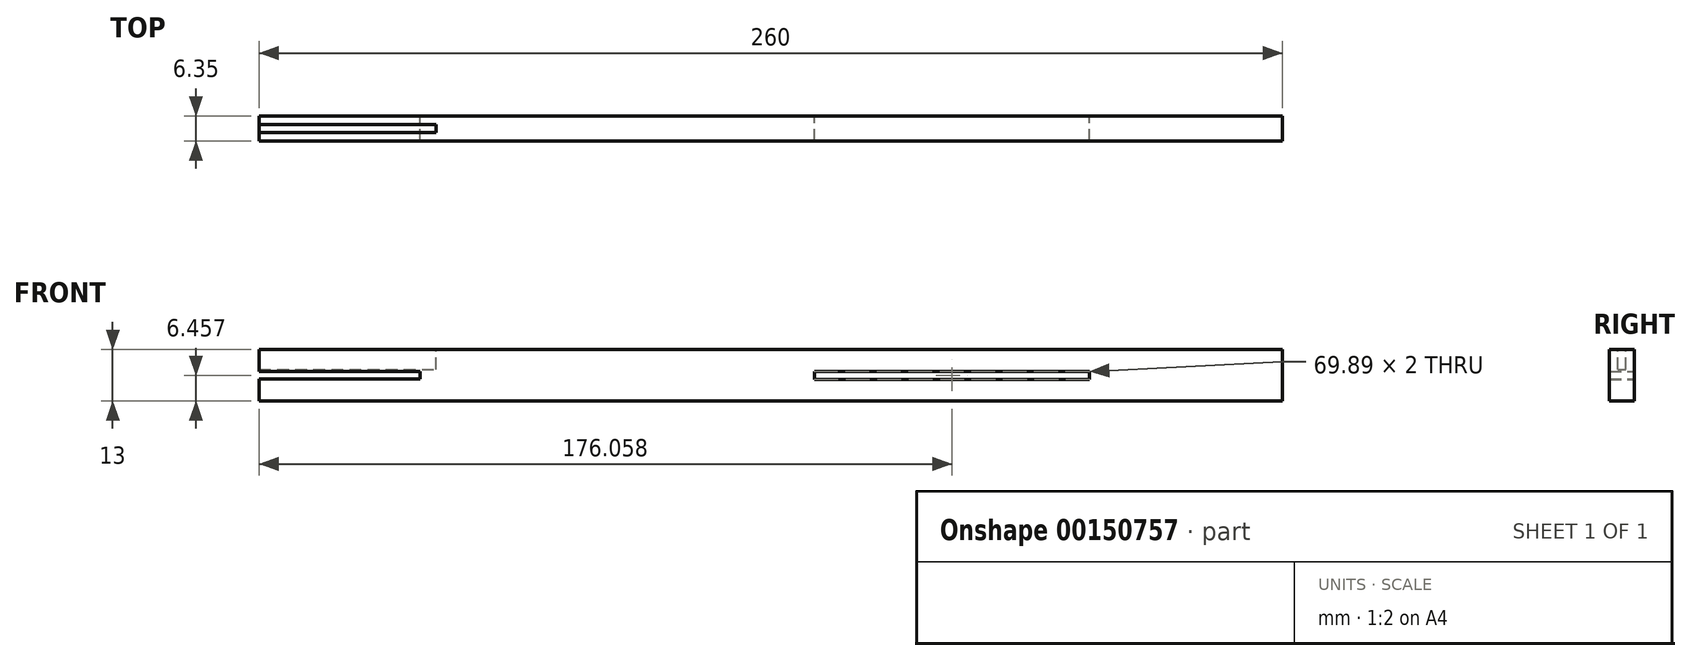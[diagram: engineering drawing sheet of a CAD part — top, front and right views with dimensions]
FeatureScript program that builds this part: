
annotation { "Feature Type Name" : "Feature", "Feature Type Description" : "" }
export const myFeature = defineFeature(function(context is Context, id is Id, definition is map)
    precondition{}
    {
        {
            var Q0;
            Q0=qCreatedBy(makeId("Front.planeOp"),FACE);
            var sketch = newSketch(context, id + "F0", { "sketchPlane" : qUnion([Q0])});
            skLineSegment(sketch, "E0.bottom", {"start": v(-130, 13) * mm, "end": v(130, 13) * mm});
            skLineSegment(sketch, "E0.top", {"start": v(-130, 0) * mm, "end": v(130, 0) * mm});
            skLineSegment(sketch, "E0.left", {"start": v(-130, 13) * mm, "end": v(-130, 7.5) * mm});
            skLineSegment(sketch, "E0.right", {"start": v(130, 13) * mm, "end": v(130, 0) * mm});
            skLineSegment(sketch, "E1.bottom", {"start": v(-130, 7.5) * mm, "end": v(-89, 7.5) * mm});
            skLineSegment(sketch, "E1.top", {"start": v(-130, 5.5) * mm, "end": v(-89, 5.5) * mm});
            skLineSegment(sketch, "E1.right", {"start": v(-89, 7.5) * mm, "end": v(-89, 5.5) * mm});
            skLineSegment(sketch, "E2.trimOffspring", {"start": v(-130, 5.5) * mm, "end": v(-130, 0) * mm});
            skLineSegment(sketch, "E3.bottom", {"start": v(11.11, 7.46) * mm, "end": v(81, 7.46) * mm});
            skLineSegment(sketch, "E3.top", {"start": v(11.11, 5.46) * mm, "end": v(81, 5.46) * mm});
            skLineSegment(sketch, "E3.left", {"start": v(11.11, 7.46) * mm, "end": v(11.11, 5.46) * mm});
            skLineSegment(sketch, "E3.right", {"start": v(81, 7.46) * mm, "end": v(81, 5.46) * mm});
            skSolve(sketch);
        }
        {
            var Q0;
            Q0=makeQuery(id+"F0.imprint","IMPRINT",FACE,{"disambiguationData":[TD([[makeQuery(id+"F0.imprint","IMPRINT",EDGE,{"derivedFrom":sQuery(id+"F0.wireOp",EDGE,"E0.bottom")}),-1.0]])]});
            extrude(context, id + "F1", {"entities" : qUnion([Q0]), "depth" : 6.35 * mm});
        }
        {
            var Q0;
            Q0=makeQuery(id+"F1.opExtrude","SWEPT_FACE",FACE,{"disambiguationData":[OSD([sQuery(id+"F0.wireOp",EDGE,"E0.bottom")])]});
            var sketch = newSketch(context, id + "F2", { "sketchPlane" : qUnion([Q0])});
            skLineSegment(sketch, "E4.bottom", {"start": v(-130, -2.17) * mm, "end": v(-85, -2.17) * mm});
            skLineSegment(sketch, "E4.top", {"start": v(-130, -4.17) * mm, "end": v(-85, -4.17) * mm});
            skLineSegment(sketch, "E4.left", {"start": v(-130, -2.17) * mm, "end": v(-130, -4.17) * mm});
            skLineSegment(sketch, "E4.right", {"start": v(-85, -2.17) * mm, "end": v(-85, -4.17) * mm});
            skSolve(sketch);
        }
        {
            var Q0;
            Q0=makeQuery(id+"F2.imprint","IMPRINT",FACE,{"disambiguationData":[TD([[makeQuery(id+"F2.imprint","IMPRINT",EDGE,{"derivedFrom":sQuery(id+"F2.wireOp",EDGE,"E4.bottom")}),-1.0]])]});
            extrude(context, id + "F3", {"entities" : qUnion([Q0]), "operationType" : NewBodyOperationType.REMOVE, "oppositeDirection" : true, "depth" : 5 * mm});
        }
    });
